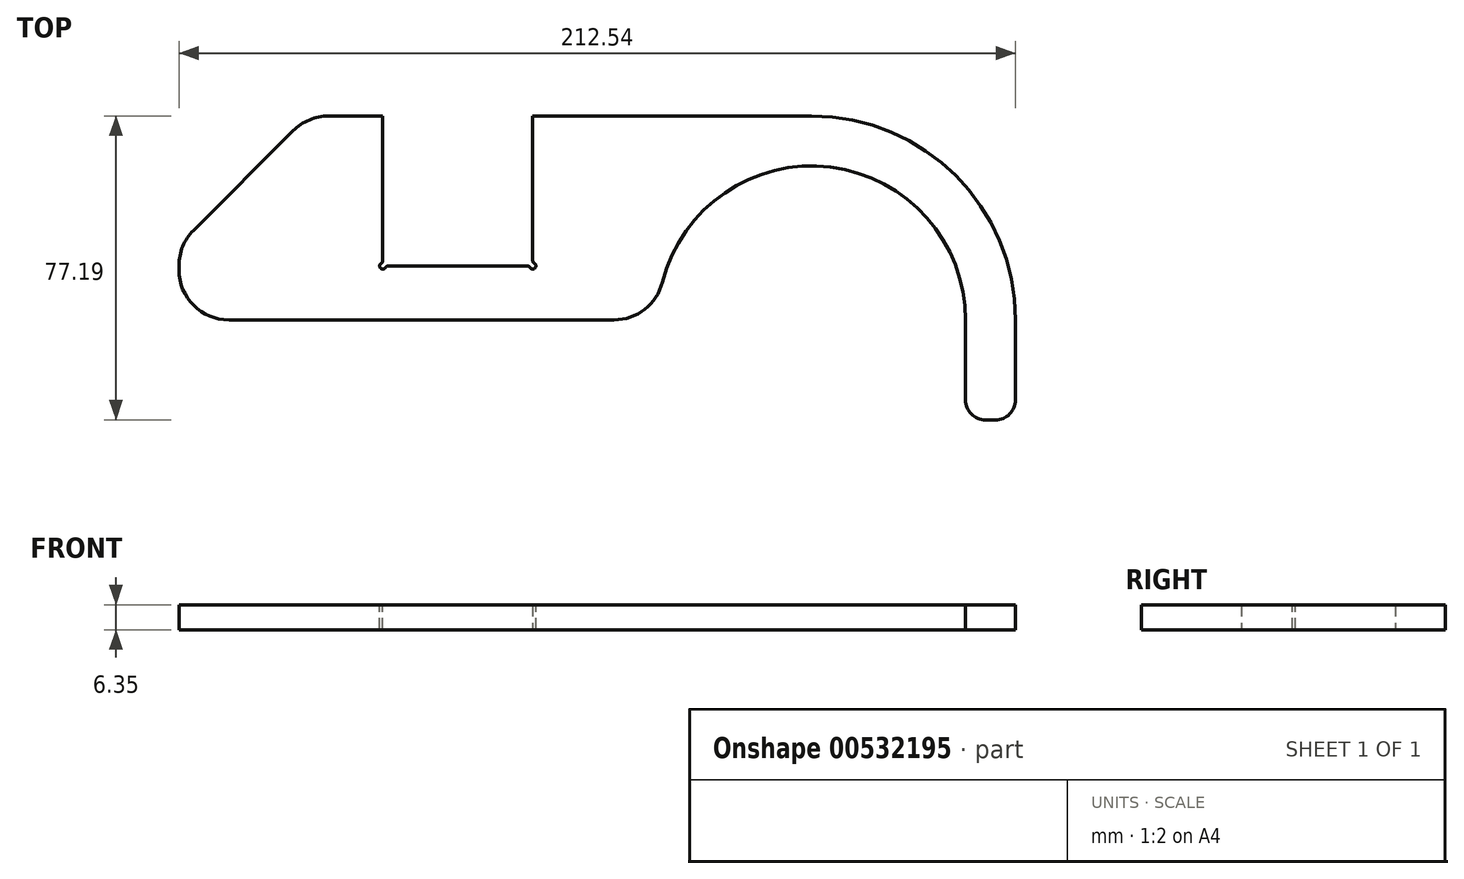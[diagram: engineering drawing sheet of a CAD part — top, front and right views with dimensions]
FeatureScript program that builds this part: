
annotation { "Feature Type Name" : "Feature", "Feature Type Description" : "" }
export const myFeature = defineFeature(function(context is Context, id is Id, definition is map)
    precondition{}
    {
        {
            var Q0;
            Q0=qCreatedBy(makeId("Top.planeOp"),FACE);
            var sketch = newSketch(context, id + "F0", { "sketchPlane" : qUnion([Q0])});
            skLineSegment(sketch, "E0", {"start": v(-70.75, 12.48) * mm, "end": v(-29.14, 41.61) * mm, "construction": true});
            skLineSegment(sketch, "E1", {"start": v(-29.14, 41.61) * mm, "end": v(0, 0) * mm, "construction": true});
            skLineSegment(sketch, "E2", {"start": v(0, 0) * mm, "end": v(-41.61, -29.14) * mm, "construction": true});
            skLineSegment(sketch, "E3", {"start": v(-41.61, -29.14) * mm, "end": v(-70.75, 12.48) * mm, "construction": true});
            skLineSegment(sketch, "E4", {"start": v(0, 0) * mm, "end": v(30.96, 0) * mm, "construction": true});
            skLineSegment(sketch, "E5", {"start": v(-70.75, 12.48) * mm, "end": v(0, 0) * mm, "construction": true});
            skLineSegment(sketch, "E6", {"start": v(-29.14, 41.61) * mm, "end": v(-41.61, -29.14) * mm, "construction": true});
            skLineSegment(sketch, "E7", {"start": v(-74.47, 6.24) * mm, "end": v(-87.17, 6.24) * mm});
            skLineSegment(sketch, "E8.trimOffspring", {"start": v(3.72, 6.24) * mm, "end": v(16.42, 6.24) * mm});
            skLineSegment(sketch, "E9", {"start": v(-106.22, 58.03) * mm, "end": v(-35.38, 58.03) * mm});
            skArc(sketch, "E10", {"start": v(-74.47, 6.24) * mm, "mid": v(-35.38, -32.86) * mm, "end": v(3.72, 6.24) * mm, "construction": true});
            skArc(sketch, "E11", {"start": v(3.72, 6.24) * mm, "mid": v(-35.38, 45.33) * mm, "end": v(-74.47, 6.24) * mm});
            skArc(sketch, "E12", {"start": v(-87.17, 6.24) * mm, "mid": v(-35.38, -45.56) * mm, "end": v(16.42, 6.24) * mm, "construction": true});
            skArc(sketch, "E13", {"start": v(16.42, 6.24) * mm, "mid": v(1.25, 42.86) * mm, "end": v(-35.38, 58.03) * mm});
            skLineSegment(sketch, "E14.bottom", {"start": v(-106.22, 19.93) * mm, "end": v(-144.32, 19.93) * mm});
            skLineSegment(sketch, "E14.top", {"start": v(-106.22, 58.03) * mm, "end": v(-144.32, 58.03) * mm, "construction": true});
            skLineSegment(sketch, "E14.left", {"start": v(-106.22, 19.93) * mm, "end": v(-106.22, 58.03) * mm});
            skLineSegment(sketch, "E14.right", {"start": v(-144.32, 19.93) * mm, "end": v(-144.32, 58.03) * mm});
            skPoint(sketch, "E14.middle", {"position": v(-125.27, 38.98) * mm});
            skLineSegment(sketch, "E15", {"start": v(-87.17, 6.24) * mm, "end": v(-196.12, 6.24) * mm});
            skLineSegment(sketch, "E16", {"start": v(-196.12, 6.24) * mm, "end": v(-196.12, 25.29) * mm});
            skLineSegment(sketch, "E17", {"start": v(-163.37, 58.03) * mm, "end": v(-144.32, 58.03) * mm});
            skArc(sketch, "E18", {"start": v(-35.38, 58.03) * mm, "mid": v(-72, 42.86) * mm, "end": v(-87.17, 6.24) * mm, "construction": true});
            skLineSegment(sketch, "E19", {"start": v(3.72, 6.24) * mm, "end": v(3.72, -19.16) * mm});
            skLineSegment(sketch, "E20", {"start": v(3.72, -19.16) * mm, "end": v(16.42, -19.16) * mm});
            skLineSegment(sketch, "E21", {"start": v(16.42, 6.24) * mm, "end": v(16.42, -19.16) * mm});
            skLineSegment(sketch, "E22", {"start": v(-196.12, 25.29) * mm, "end": v(-163.37, 58.03) * mm});
            skSolve(sketch);
        }
        {
            var Q0;
            Q0 = qSketchRegion(id + "F0", true);
            extrude(context, id + "F1", {"entities" : qUnion([Q0]), "depth" : 6.35 * mm, "offsetDistance" : 25.4 * mm});
        }
        {
            var Q0;
            Q0=makeQuery(id+"F1.opExtrude","SWEPT_EDGE",EDGE,{"disambiguationData":[OSD([sQuery(id+"F0.wireOp",EDGE,"E20"),sQuery(id+"F0.wireOp",EDGE,"E21")])]});
            var Q1;
            Q1=makeQuery(id+"F1.opExtrude","SWEPT_EDGE",EDGE,{"disambiguationData":[OSD([sQuery(id+"F0.wireOp",EDGE,"E19"),sQuery(id+"F0.wireOp",EDGE,"E20")])]});
            fillet(context, id + "F2", {"entities" : qUnion([Q0, Q1]), "radius" : 5.08 * mm, "tangentPropagation" : true, "allowEdgeOverflow" : false});
        }
        {
            var Q0;
            Q0=makeQuery(id+"F1.opExtrude","SWEPT_EDGE",EDGE,{"disambiguationData":[OSD([sQuery(id+"F0.wireOp",EDGE,"E7"),sQuery(id+"F0.wireOp",EDGE,"E11")])]});
            var Q1;
            Q1=makeQuery(id+"F1.opExtrude","SWEPT_EDGE",EDGE,{"disambiguationData":[OSD([sQuery(id+"F0.wireOp",EDGE,"E16"),sQuery(id+"F0.wireOp",EDGE,"E22")])]});
            var Q2;
            Q2=makeQuery(id+"F1.opExtrude","SWEPT_EDGE",EDGE,{"disambiguationData":[OSD([sQuery(id+"F0.wireOp",EDGE,"E17"),sQuery(id+"F0.wireOp",EDGE,"E22")])]});
            var Q3;
            Q3=makeQuery(id+"F1.opExtrude","SWEPT_EDGE",EDGE,{"disambiguationData":[OSD([sQuery(id+"F0.wireOp",EDGE,"E15"),sQuery(id+"F0.wireOp",EDGE,"E16")])]});
            fillet(context, id + "F3", {"entities" : qUnion([Q0, Q1, Q2, Q3]), "radius" : 12.7 * mm, "tangentPropagation" : true, "allowEdgeOverflow" : false});
        }
        {
            var Q0;
            Q0=makeQuery(id+"F1.opExtrude","CAP_FACE",FACE,{"disambiguationData":[OSD([sQuery(id+"F0.wireOp",EDGE,"E7"),sQuery(id+"F0.wireOp",EDGE,"E9"),sQuery(id+"F0.wireOp",EDGE,"E11"),sQuery(id+"F0.wireOp",EDGE,"E13"),sQuery(id+"F0.wireOp",EDGE,"E14.bottom"),sQuery(id+"F0.wireOp",EDGE,"E14.left"),sQuery(id+"F0.wireOp",EDGE,"E14.right"),sQuery(id+"F0.wireOp",EDGE,"E15"),sQuery(id+"F0.wireOp",EDGE,"E16"),sQuery(id+"F0.wireOp",EDGE,"E17"),sQuery(id+"F0.wireOp",EDGE,"E19"),sQuery(id+"F0.wireOp",EDGE,"E20"),sQuery(id+"F0.wireOp",EDGE,"E21"),sQuery(id+"F0.wireOp",EDGE,"E22")])],"isStart":false});
            var sketch = newSketch(context, id + "F4", { "sketchPlane" : qUnion([Q0])});
            skArc(sketch, "E23", {"start": v(-144.72, 20.62) * mm, "mid": v(-144.88, 19.37) * mm, "end": v(-143.63, 19.54) * mm});
            skArc(sketch, "E24", {"start": v(-144.72, 20.62) * mm, "mid": v(-144.43, 20.91) * mm, "end": v(-144.32, 21.3) * mm});
            skArc(sketch, "E25", {"start": v(-142.95, 19.93) * mm, "mid": v(-143.34, 19.83) * mm, "end": v(-143.63, 19.54) * mm});
            skLineSegment(sketch, "E26", {"start": v(-144.32, 21.3) * mm, "end": v(-142.95, 19.93) * mm});
            skLineSegment(sketch, "E27", {"start": v(-125.27, 19.93) * mm, "end": v(-125.27, 44.68) * mm, "construction": true});
            skLineSegment(sketch, "E28.MirrorCS", {"start": v(-106.22, 21.3) * mm, "end": v(-107.6, 19.93) * mm});
            skArc(sketch, "E29.MirrorCS", {"start": v(-107.6, 19.93) * mm, "mid": v(-107.2, 19.83) * mm, "end": v(-106.9, 19.54) * mm});
            skArc(sketch, "E30.MirrorCS", {"start": v(-105.82, 20.62) * mm, "mid": v(-105.66, 19.37) * mm, "end": v(-106.9, 19.54) * mm});
            skArc(sketch, "E31.MirrorCS", {"start": v(-105.82, 20.62) * mm, "mid": v(-106.11, 20.91) * mm, "end": v(-106.22, 21.3) * mm});
            skSolve(sketch);
        }
        {
            var Q0;
            Q0 = qSketchRegion(id + "F4", true);
            extrude(context, id + "F5", {"entities" : qUnion([Q0]), "operationType" : NewBodyOperationType.REMOVE, "endBound" : BoundingType.THROUGH_ALL, "oppositeDirection" : true, "depth" : 25.4 * mm, "offsetDistance" : 25.4 * mm});
        }
    });
